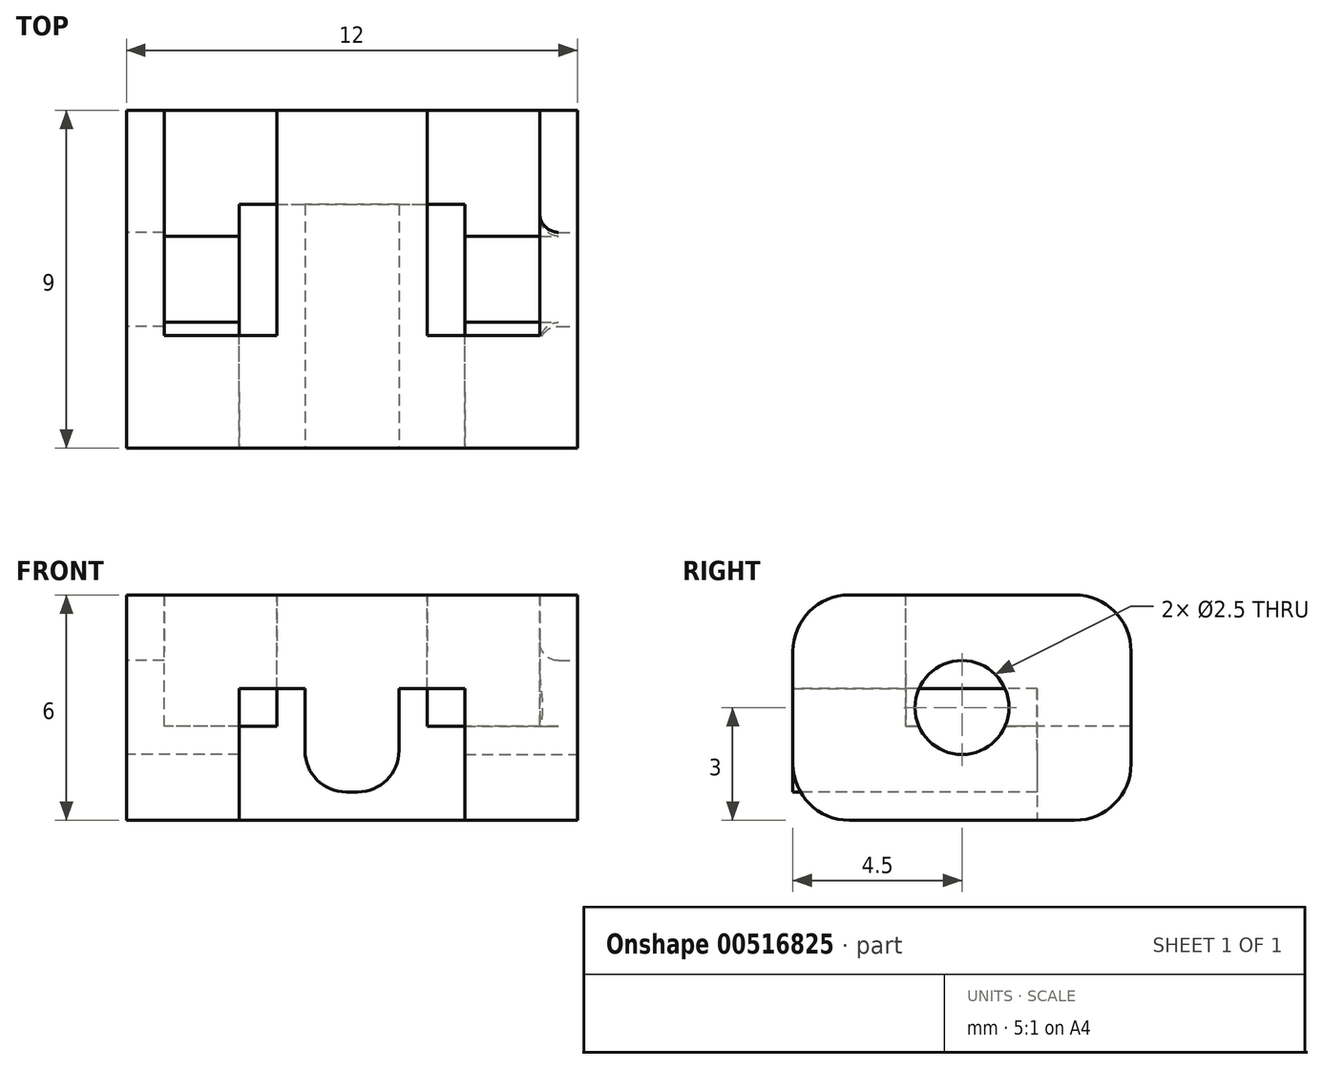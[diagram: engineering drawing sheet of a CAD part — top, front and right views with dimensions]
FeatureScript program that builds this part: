
annotation { "Feature Type Name" : "Feature", "Feature Type Description" : "" }
export const myFeature = defineFeature(function(context is Context, id is Id, definition is map)
    precondition{}
    {
        {
            var Q0;
            Q0=qCreatedBy(makeId("Top.planeOp"),FACE);
            var sketch = newSketch(context, id + "F0", { "sketchPlane" : qUnion([Q0])});
            skLineSegment(sketch, "E0.bottom", {"start": v(6, -4.5) * mm, "end": v(-6, -4.5) * mm});
            skLineSegment(sketch, "E0.top", {"start": v(6, 4.5) * mm, "end": v(-6, 4.5) * mm});
            skLineSegment(sketch, "E0.left", {"start": v(6, -4.5) * mm, "end": v(6, 4.5) * mm});
            skLineSegment(sketch, "E0.right", {"start": v(-6, -4.5) * mm, "end": v(-6, 4.5) * mm});
            skPoint(sketch, "E0.middle", {"position": v(0, 0) * mm});
            skSolve(sketch);
        }
        {
            var Q0;
            Q0 = qSketchRegion(id + "F0", true);
            extrude(context, id + "F1", {"entities" : qUnion([Q0]), "depth" : 6 * mm, "offsetDistance" : 25 * mm});
        }
        {
            var Q0;
            Q0=makeQuery(id+"F1.opExtrude","CAP_FACE",FACE,{"disambiguationData":[OSD([sQuery(id+"F0.wireOp",EDGE,"E0.bottom"),sQuery(id+"F0.wireOp",EDGE,"E0.top"),sQuery(id+"F0.wireOp",EDGE,"E0.left"),sQuery(id+"F0.wireOp",EDGE,"E0.right")])],"isStart":false});
            var sketch = newSketch(context, id + "F2", { "sketchPlane" : qUnion([Q0])});
            skLineSegment(sketch, "E1.bottom", {"start": v(-5, 4.5) * mm, "end": v(-2, 4.5) * mm});
            skLineSegment(sketch, "E1.top", {"start": v(-5, -1.5) * mm, "end": v(-2, -1.5) * mm});
            skLineSegment(sketch, "E1.left", {"start": v(-5, 4.5) * mm, "end": v(-5, -1.5) * mm});
            skLineSegment(sketch, "E1.right", {"start": v(-2, 4.5) * mm, "end": v(-2, -1.5) * mm});
            skLineSegment(sketch, "E2.bottom", {"start": v(5, 4.5) * mm, "end": v(2, 4.5) * mm});
            skLineSegment(sketch, "E2.top", {"start": v(5, -1.5) * mm, "end": v(2, -1.5) * mm});
            skLineSegment(sketch, "E2.left", {"start": v(5, 4.5) * mm, "end": v(5, -1.5) * mm});
            skLineSegment(sketch, "E2.right", {"start": v(2, 4.5) * mm, "end": v(2, -1.5) * mm});
            skSolve(sketch);
        }
        {
            var Q0;
            Q0=makeQuery(id+"F2.imprint","IMPRINT",FACE,{"disambiguationData":[TD([[makeQuery(id+"F2.imprint","IMPRINT",EDGE,{"derivedFrom":sQuery(id+"F2.wireOp",EDGE,"E2.bottom")}),1.0]])]});
            var Q1;
            Q1=makeQuery(id+"F2.imprint","IMPRINT",FACE,{"disambiguationData":[TD([[makeQuery(id+"F2.imprint","IMPRINT",EDGE,{"derivedFrom":sQuery(id+"F2.wireOp",EDGE,"E1.bottom")}),1.0]])]});
            extrude(context, id + "F3", {"entities" : qUnion([Q0, Q1]), "operationType" : NewBodyOperationType.REMOVE, "oppositeDirection" : true, "depth" : 3.5 * mm, "offsetDistance" : 25 * mm});
        }
        {
            var Q0;
            Q0=makeQuery(id+"F1.opExtrude","CAP_FACE",FACE,{"disambiguationData":[OSD([sQuery(id+"F0.wireOp",EDGE,"E0.bottom"),sQuery(id+"F0.wireOp",EDGE,"E0.top"),sQuery(id+"F0.wireOp",EDGE,"E0.left"),sQuery(id+"F0.wireOp",EDGE,"E0.right")])],"isStart":true});
            var sketch = newSketch(context, id + "F4", { "sketchPlane" : qUnion([Q0])});
            skLineSegment(sketch, "E3.bottom", {"start": v(-3, 4.5) * mm, "end": v(3, 4.5) * mm});
            skLineSegment(sketch, "E3.top", {"start": v(-3, -2) * mm, "end": v(3, -2) * mm});
            skLineSegment(sketch, "E3.left", {"start": v(-3, 4.5) * mm, "end": v(-3, -2) * mm});
            skLineSegment(sketch, "E3.right", {"start": v(3, 4.5) * mm, "end": v(3, -2) * mm});
            skSolve(sketch);
        }
        {
            var Q0;
            Q0 = qSketchRegion(id + "F4", true);
            extrude(context, id + "F5", {"entities" : qUnion([Q0]), "operationType" : NewBodyOperationType.REMOVE, "oppositeDirection" : true, "depth" : 3.5 * mm, "offsetDistance" : 25 * mm});
        }
        {
            var Q0;
            Q0=makeQuery(id+"F1.opExtrude","SWEPT_FACE",FACE,{"disambiguationData":[OSD([sQuery(id+"F0.wireOp",EDGE,"E0.left")])]});
            var sketch = newSketch(context, id + "F6", { "sketchPlane" : qUnion([Q0])});
            skLineSegment(sketch, "E4", {"start": v(0, 6) * mm, "end": v(0, 0) * mm, "construction": true});
            skLineSegment(sketch, "E5", {"start": v(-4.5, 3) * mm, "end": v(4.5, 3) * mm, "construction": true});
            skCircle(sketch, "E6", {"center": v(0, 3) * mm, "radius": 1.25 * mm});
            skSolve(sketch);
        }
        {
            var Q0;
            Q0 = qSketchRegion(id + "F6", true);
            extrude(context, id + "F7", {"entities" : qUnion([Q0]), "operationType" : NewBodyOperationType.REMOVE, "oppositeDirection" : true, "depth" : 3 * mm, "offsetDistance" : 25 * mm});
        }
        {
            var Q0;
            Q0=makeQuery(id+"F1.opExtrude","SWEPT_FACE",FACE,{"disambiguationData":[OSD([sQuery(id+"F0.wireOp",EDGE,"E0.right")])]});
            var sketch = newSketch(context, id + "F8", { "sketchPlane" : qUnion([Q0])});
            skLineSegment(sketch, "E7", {"start": v(-4.5, 3) * mm, "end": v(4.5, 3) * mm, "construction": true});
            skLineSegment(sketch, "E8", {"start": v(0, 6) * mm, "end": v(0, 0) * mm, "construction": true});
            skCircle(sketch, "E9", {"center": v(0, 3) * mm, "radius": 1.25 * mm});
            skSolve(sketch);
        }
        {
            var Q0;
            Q0 = qSketchRegion(id + "F8", true);
            extrude(context, id + "F9", {"entities" : qUnion([Q0]), "operationType" : NewBodyOperationType.REMOVE, "endBound" : BoundingType.UP_TO_NEXT, "oppositeDirection" : true, "depth" : 3 * mm, "offsetDistance" : 25 * mm});
        }
        {
            var Q0;
            Q0=makeQuery(id+"F3.boolean.opBoolean","COPY",EDGE,{"derivedFrom":makeQuery(id+"F3.opExtrude","CAP_EDGE",EDGE,{"disambiguationData":[OSD([sQuery(id+"F2.wireOp",EDGE,"E2.right")])],"isStart":true})});
            var Q1;
            Q1=makeQuery(id+"F3.boolean.opBoolean","COPY",EDGE,{"derivedFrom":makeQuery(id+"F3.opExtrude","CAP_EDGE",EDGE,{"disambiguationData":[OSD([sQuery(id+"F2.wireOp",EDGE,"E1.right")])],"isStart":true})});
            var Q2;
            Q2=makeQuery(id+"F1.opExtrude","CAP_EDGE",EDGE,{"disambiguationData":[OSD([sQuery(id+"F0.wireOp",EDGE,"E0.bottom")])],"isStart":false});
            var Q3;
            {var subQ0=sQuery(id+"F0.wireOp",EDGE,"E0.bottom");var subQ1=sQuery(id+"F0.wireOp",EDGE,"E0.right");Q3=makeQuery(id+"F5.boolean.opBoolean","SPLIT",EDGE,{"disambiguationData":[TD([makeQuery(id+"F1.opExtrude","SWEPT_FACE",FACE,{"disambiguationData":[OSD([subQ1])]})])],"derivedFrom":makeQuery(id+"F1.opExtrude","CAP_EDGE",EDGE,{"disambiguationData":[OSD([subQ0])],"isStart":true})});}
            var Q4;
            {var subQ0=sQuery(id+"F0.wireOp",EDGE,"E0.bottom");var subQ1=sQuery(id+"F0.wireOp",EDGE,"E0.left");Q4=makeQuery(id+"F5.boolean.opBoolean","SPLIT",EDGE,{"disambiguationData":[TD([makeQuery(id+"F1.opExtrude","SWEPT_FACE",FACE,{"disambiguationData":[OSD([subQ1])]})])],"derivedFrom":makeQuery(id+"F1.opExtrude","CAP_EDGE",EDGE,{"disambiguationData":[OSD([subQ0])],"isStart":true})});}
            var Q5;
            Q5=makeQuery(id+"F1.opExtrude","CAP_EDGE",EDGE,{"disambiguationData":[OSD([sQuery(id+"F0.wireOp",EDGE,"E0.top")])],"isStart":true});
            var Q6;
            {var subQ0=sQuery(id+"F0.wireOp",EDGE,"E0.right");var subQ1=sQuery(id+"F0.wireOp",EDGE,"E0.top");Q6=makeQuery(id+"F3.boolean.opBoolean","SPLIT",EDGE,{"disambiguationData":[TD([makeQuery(id+"F1.opExtrude","SWEPT_FACE",FACE,{"disambiguationData":[OSD([subQ0])]})])],"derivedFrom":makeQuery(id+"F1.opExtrude","CAP_EDGE",EDGE,{"disambiguationData":[OSD([subQ1])],"isStart":false})});}
            var Q7;
            {var subQ0=sQuery(id+"F0.wireOp",EDGE,"E0.left");var subQ1=sQuery(id+"F0.wireOp",EDGE,"E0.top");Q7=makeQuery(id+"F3.boolean.opBoolean","SPLIT",EDGE,{"disambiguationData":[TD([makeQuery(id+"F1.opExtrude","SWEPT_FACE",FACE,{"disambiguationData":[OSD([subQ0])]})])],"derivedFrom":makeQuery(id+"F1.opExtrude","CAP_EDGE",EDGE,{"disambiguationData":[OSD([subQ1])],"isStart":false})});}
            var Q8;
            {var subQ0=sQuery(id+"F0.wireOp",EDGE,"E0.top");Q8=makeQuery(id+"F3.boolean.opBoolean","SPLIT",EDGE,{"disambiguationData":[TD([makeQuery(id+"F3.opExtrude","SWEPT_FACE",FACE,{"disambiguationData":[OSD([sQuery(id+"F2.wireOp",EDGE,"E1.right")])]})])],"derivedFrom":makeQuery(id+"F1.opExtrude","CAP_EDGE",EDGE,{"disambiguationData":[OSD([subQ0])],"isStart":false})});}
            fillet(context, id + "F10", {"entities" : qUnion([Q0, Q1, Q2, Q3, Q4, Q5, Q6, Q7, Q8]), "radius" : 1.5 * mm, "tangentPropagation" : true, "allowEdgeOverflow" : false});
        }
        {
            var Q0;
            Q0=makeQuery(id+"F5.boolean.opBoolean","COPY",FACE,{"derivedFrom":makeQuery(id+"F5.opExtrude","CAP_FACE",FACE,{"disambiguationData":[OSD([sQuery(id+"F4.wireOp",EDGE,"E3.bottom"),sQuery(id+"F4.wireOp",EDGE,"E3.top"),sQuery(id+"F4.wireOp",EDGE,"E3.left"),sQuery(id+"F4.wireOp",EDGE,"E3.right")])],"isStart":false})});
            var sketch = newSketch(context, id + "F11", { "sketchPlane" : qUnion([Q0])});
            skLineSegment(sketch, "E10.bottom", {"start": v(-1.25, -2) * mm, "end": v(1.25, -2) * mm});
            skLineSegment(sketch, "E10.top", {"start": v(-1.25, 4.5) * mm, "end": v(1.25, 4.5) * mm});
            skLineSegment(sketch, "E10.left", {"start": v(-1.25, -2) * mm, "end": v(-1.25, 4.5) * mm});
            skLineSegment(sketch, "E10.right", {"start": v(1.25, -2) * mm, "end": v(1.25, 4.5) * mm});
            skSolve(sketch);
        }
        {
            var Q0;
            Q0 = qSketchRegion(id + "F11", true);
            extrude(context, id + "F12", {"entities" : qUnion([Q0]), "operationType" : NewBodyOperationType.ADD, "depth" : 2.75 * mm, "offsetDistance" : 25 * mm});
        }
        {
            var Q0;
            Q0=makeQuery(id+"F12.opExtrude","CAP_EDGE",EDGE,{"disambiguationData":[OSD([sQuery(id+"F11.wireOp",EDGE,"E10.left")])],"isStart":false});
            var Q1;
            Q1=makeQuery(id+"F12.opExtrude","CAP_EDGE",EDGE,{"disambiguationData":[OSD([sQuery(id+"F11.wireOp",EDGE,"E10.right")])],"isStart":false});
            fillet(context, id + "F13", {"entities" : qUnion([Q0, Q1]), "radius" : 1.1 * mm, "tangentPropagation" : true, "allowEdgeOverflow" : false});
        }
        {
            var Q0;
            Q0=makeQuery(id+"F7.boolean.opBoolean","COPY",EDGE,{"derivedFrom":makeQuery(id+"F7.opExtrude","CAP_EDGE",EDGE,{"disambiguationData":[OSD([sQuery(id+"F6.wireOp",EDGE,"E6")])],"isStart":true})});
            var Q1;
            Q1=makeQuery(id+"F9.boolean.opBoolean","COPY",EDGE,{"derivedFrom":makeQuery(id+"F9.opExtrude","CAP_EDGE",EDGE,{"disambiguationData":[OSD([sQuery(id+"F8.wireOp",EDGE,"E9")])],"isStart":true})});
            var Q2;
            Q2=makeQuery(id+"F9.boolean.opBoolean","COPY",EDGE,{"derivedFrom":makeQuery(id+"F9.opExtrude","CAP_EDGE",EDGE,{"disambiguationData":[OSD([sQuery(id+"F8.wireOp",EDGE,"E9")]),topologyDisambiguationEdgeConnected([makeQuery(id+"F3.boolean.opBoolean","COPY",FACE,{"derivedFrom":makeQuery(id+"F3.opExtrude","SWEPT_FACE",FACE,{"disambiguationData":[OSD([sQuery(id+"F2.wireOp",EDGE,"E1.left")])]})})])],"isStart":false})});
            var Q3;
            Q3=makeQuery(id+"F7.boolean.opBoolean","INTERSECT",EDGE,{"derivedFrom":[makeQuery(id+"F3.boolean.opBoolean","COPY",FACE,{"derivedFrom":makeQuery(id+"F3.opExtrude","SWEPT_FACE",FACE,{"disambiguationData":[OSD([sQuery(id+"F2.wireOp",EDGE,"E2.left")])]})}),makeQuery(id+"F7.opExtrude","SWEPT_FACE",FACE,{"disambiguationData":[OSD([sQuery(id+"F6.wireOp",EDGE,"E6")])]})]});
            var Q4;
            Q4=makeQuery(id+"F7.boolean.opBoolean","COPY",EDGE,{"derivedFrom":makeQuery(id+"F7.opExtrude","CAP_EDGE",EDGE,{"disambiguationData":[OSD([sQuery(id+"F6.wireOp",EDGE,"E6")])],"isStart":false})});
            var Q5;
            Q5=makeQuery(id+"F9.boolean.opBoolean","COPY",EDGE,{"derivedFrom":makeQuery(id+"F9.opExtrude","CAP_EDGE",EDGE,{"disambiguationData":[OSD([sQuery(id+"F8.wireOp",EDGE,"E9")]),topologyDisambiguationEdgeConnected([makeQuery(id+"F5.boolean.opBoolean","COPY",FACE,{"derivedFrom":makeQuery(id+"F5.opExtrude","SWEPT_FACE",FACE,{"disambiguationData":[OSD([sQuery(id+"F4.wireOp",EDGE,"E3.left")])]})})])],"isStart":false})});
            fillet(context, id + "F14", {"entities" : qUnion([Q0, Q1, Q2, Q3, Q4, Q5]), "radius" : .5 * mm, "tangentPropagation" : true, "allowEdgeOverflow" : false});
        }
    });
